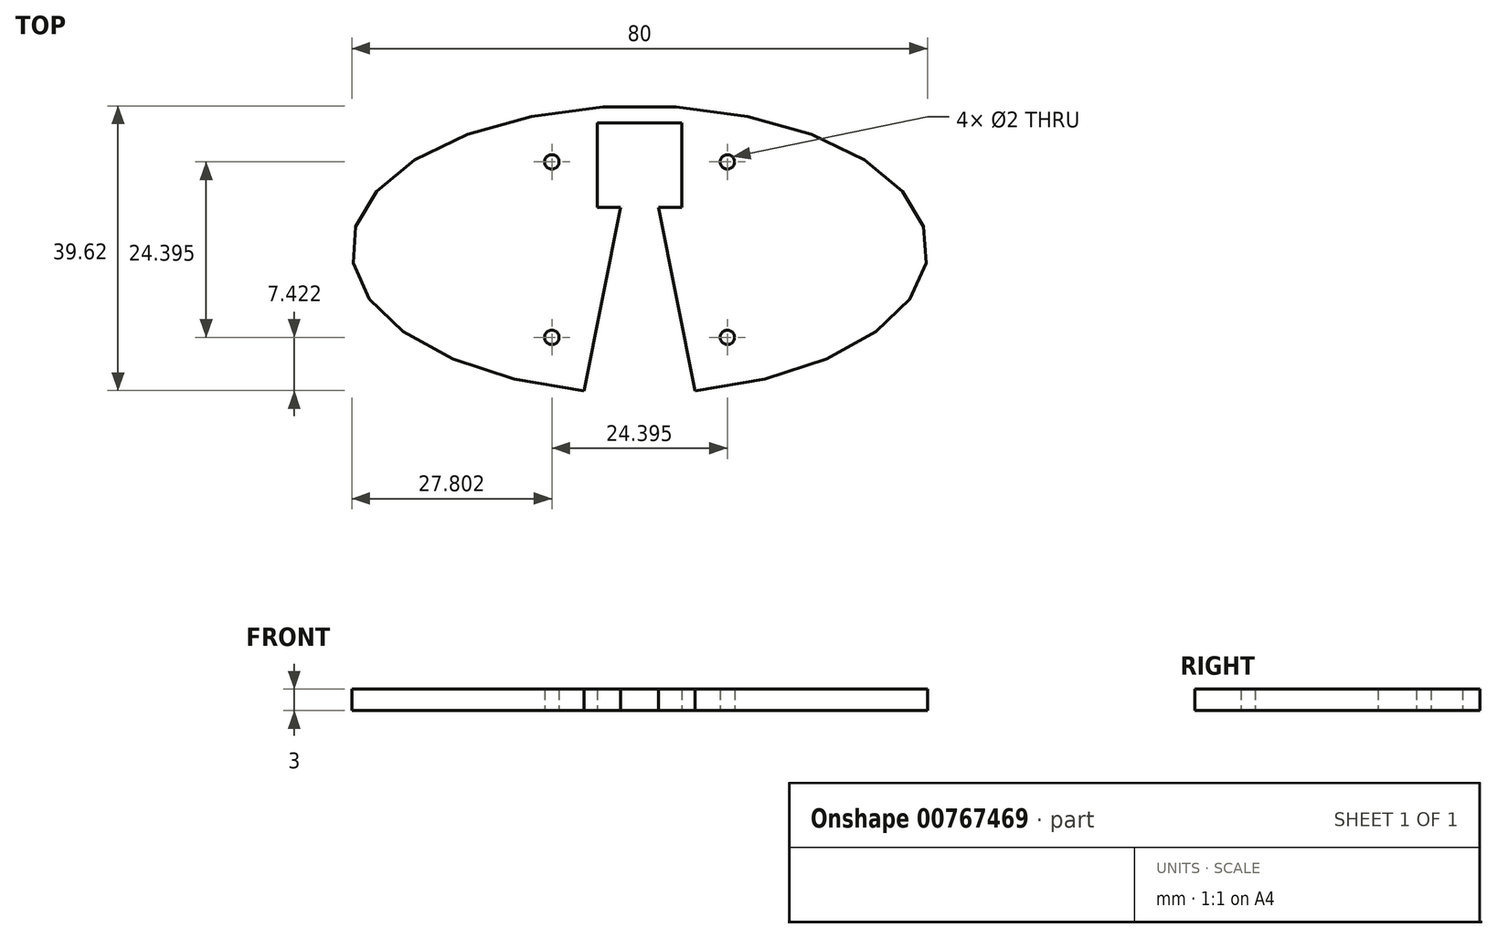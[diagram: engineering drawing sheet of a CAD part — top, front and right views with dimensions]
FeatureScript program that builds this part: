
annotation { "Feature Type Name" : "Feature", "Feature Type Description" : "" }
export const myFeature = defineFeature(function(context is Context, id is Id, definition is map)
    precondition{}
    {
        {
            var Q0;
            Q0=qCreatedBy(makeId("Top.planeOp"),FACE);
            var sketch = newSketch(context, id + "F0", { "sketchPlane" : qUnion([Q0])});
            skEllipse(sketch, "E0", {"center": v(0, 0) * mm, "majorRadius": 40 * mm, "minorRadius": 20 * mm, "majorAxis": v(1, 0)});
            skLineSegment(sketch, "E1", {"start": v(0, 0) * mm, "end": v(0, -20) * mm, "construction": true});
            skCircle(sketch, "E2", {"center": v(0, 0) * mm, "radius": 17.25 * mm, "construction": true});
            skLineSegment(sketch, "E3", {"start": v(0, 17.25) * mm, "end": v(0, 11.75) * mm, "construction": true});
            skLineSegment(sketch, "E4.bottom", {"start": v(-5.87, 17.62) * mm, "end": v(5.88, 17.62) * mm});
            skLineSegment(sketch, "E4.top", {"start": v(-5.88, 5.88) * mm, "end": v(5.88, 5.88) * mm});
            skLineSegment(sketch, "E4.left", {"start": v(-5.87, 17.62) * mm, "end": v(-5.88, 5.88) * mm});
            skLineSegment(sketch, "E4.right", {"start": v(5.88, 17.62) * mm, "end": v(5.88, 5.88) * mm});
            skPoint(sketch, "E4.middle", {"position": v(0, 11.75) * mm});
            skLineSegment(sketch, "E5", {"start": v(-2.65, 5.87) * mm, "end": v(-7.73, -19.62) * mm});
            skLineSegment(sketch, "E6", {"start": v(2.65, 5.88) * mm, "end": v(7.73, -19.62) * mm});
            skLineSegment(sketch, "E7", {"start": v(0, 0) * mm, "end": v(18.12, 18.12) * mm, "construction": true});
            skCircle(sketch, "E8", {"center": v(12.2, 12.2) * mm, "radius": 1 * mm});
            skCircle(sketch, "E9.MirrorC", {"center": v(12.2, -12.2) * mm, "radius": 1 * mm});
            skCircle(sketch, "E10.MirrorC", {"center": v(-12.2, 12.2) * mm, "radius": 1 * mm});
            skCircle(sketch, "E11.MirrorC", {"center": v(-12.2, -12.2) * mm, "radius": 1 * mm});
            skSolve(sketch);
        }
        {
            var Q0;
            Q0=makeQuery(id+"F0.imprint","IMPRINT",FACE,{"disambiguationData":[TD([[makeQuery(id+"F0.imprint","IMPRINT",EDGE,{"derivedFrom":sQuery(id+"F0.wireOp",EDGE,"E4.bottom")}),1.0]])]});
            extrude(context, id + "F1", {"entities" : qUnion([Q0]), "depth" : 3 * mm, "offsetDistance" : 25 * mm});
        }
    });
